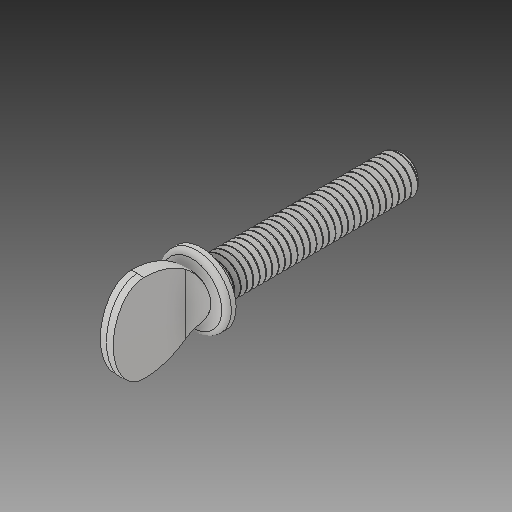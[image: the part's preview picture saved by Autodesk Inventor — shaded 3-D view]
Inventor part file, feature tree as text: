
AUTODESK INVENTOR PART (.ipt)
format: ipt  version: 2018 (Build 220112000, 112)  size: 988,672 bytes
history: native  units: in
note: dims shown in document units (in); Inventor stores cm internally (conversion verified against a paired STEP export)
features: fillet x1
ambient origin geometry x8: Origin, YZ Plane, XZ Plane, XY Plane, X Axis, Y Axis, Z Axis, Center Point
bodies: Solid1 (feature_tree)
feature tree (1):
  fillet  "Fillet14"  [1 undecoded]
note: 1 required parameter value undecoded (feature->parameter linkage not recoverable at this tier; creation-order binding heuristic only, values carry confidence <= 0.55)
